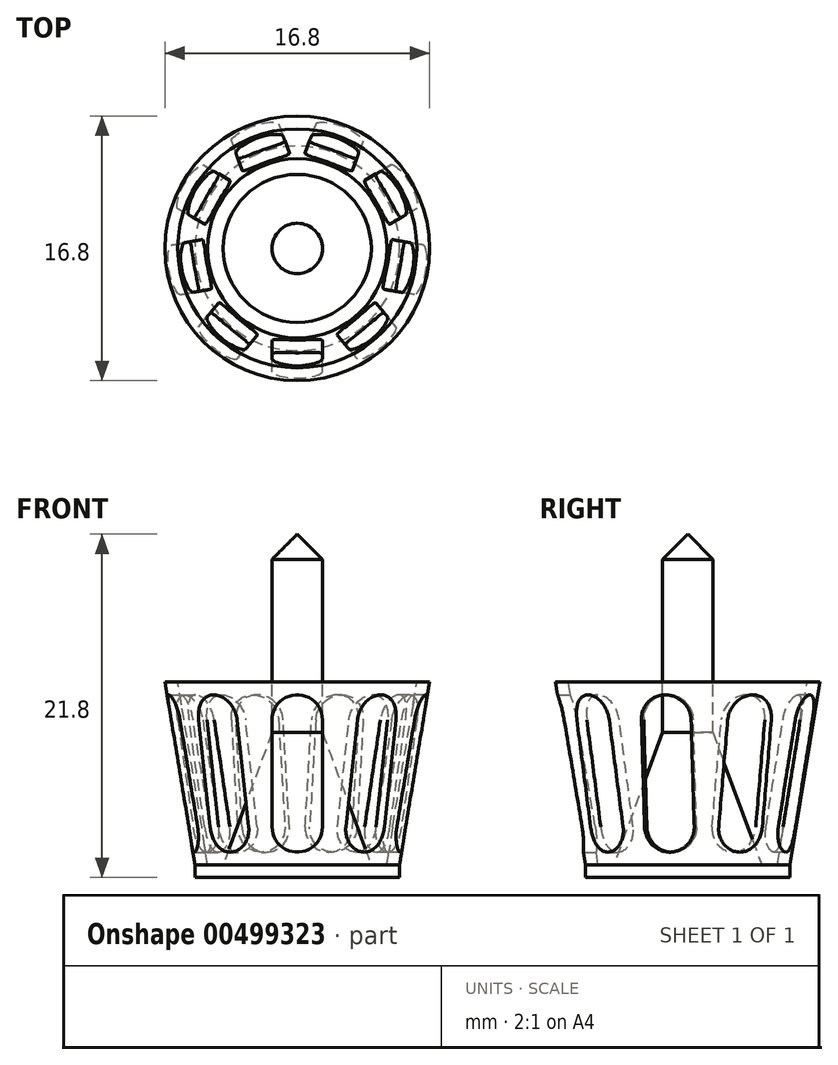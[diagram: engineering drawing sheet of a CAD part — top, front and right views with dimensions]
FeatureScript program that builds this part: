
annotation { "Feature Type Name" : "Feature", "Feature Type Description" : "" }
export const myFeature = defineFeature(function(context is Context, id is Id, definition is map)
    precondition{}
    {
        {
            var Q0;
            Q0=qCreatedBy(makeId("Top.planeOp"),FACE);
            var sketch = newSketch(context, id + "F0", { "sketchPlane" : qUnion([Q0])});
            skCircle(sketch, "E0", {"center": v(0, 0) * mm, "radius": 6.5 * mm});
            skSolve(sketch);
        }
        {
            var Q0;
            Q0=qSketchRegion(id+"F0",true);
            extrude(context, id + "F1", {"entities" : qUnion([Q0]), "depth" : 0.8 * mm});
        }
        {
            var Q0;
            Q0=qCreatedBy(makeId("Front.planeOp"),FACE);
            var sketch = newSketch(context, id + "F2", { "sketchPlane" : qUnion([Q0])});
            skLineSegment(sketch, "E1.0", {"start": v(-6.5, 0.8) * mm, "end": v(6.5, 0.8) * mm, "construction": true});
            skLineSegment(sketch, "E2", {"start": v(0, 0.8) * mm, "end": v(4.7, 0.8) * mm});
            skLineSegment(sketch, "E3", {"start": v(4.7, 0.8) * mm, "end": v(1.6, 9.2) * mm});
            skLineSegment(sketch, "E4", {"start": v(1.6, 9.2) * mm, "end": v(1.6, 20.2) * mm});
            skLineSegment(sketch, "E5", {"start": v(1.6, 20.2) * mm, "end": v(0, 21.8) * mm});
            skLineSegment(sketch, "E6", {"start": v(0, 21.8) * mm, "end": v(0, 0.8) * mm});
            skLineSegment(sketch, "E7", {"start": v(0, 23.8) * mm, "end": v(0, -5.26) * mm, "construction": true});
            skSolve(sketch);
        }
        {
            var Q0;
            Q0=qSketchRegion(id+"F2",true);
            var Q1;
            Q1=sQuery(id+"F2.wireOp",EDGE,"E7");
            revolve(context, id + "F3", {"operationType" : NewBodyOperationType.ADD, "entities" : qUnion([Q0]), "axis" : qUnion([Q1]), "revolveType" : RevolveType.FULL});
        }
        {
            var Q0;
            Q0=qCreatedBy(makeId("Front.planeOp"),FACE);
            var sketch = newSketch(context, id + "F4", { "sketchPlane" : qUnion([Q0])});
            skLineSegment(sketch, "E8.0", {"start": v(-6.5, 0.8) * mm, "end": v(6.5, 0.8) * mm, "construction": true});
            skLineSegment(sketch, "E9", {"start": v(6.5, 0.8) * mm, "end": v(8.4, 12.4) * mm});
            skLineSegment(sketch, "E10", {"start": v(8.4, 12.4) * mm, "end": v(7.59, 12.4) * mm});
            skLineSegment(sketch, "E11", {"start": v(7.59, 12.4) * mm, "end": v(5.69, 0.8) * mm});
            skLineSegment(sketch, "E12", {"start": v(5.69, 0.8) * mm, "end": v(6.5, 0.8) * mm});
            skLineSegment(sketch, "E13", {"start": v(0, 18.23) * mm, "end": v(0, -3.28) * mm, "construction": true});
            skSolve(sketch);
        }
        {
            var Q0;
            Q0=qSketchRegion(id+"F4",true);
            var Q1;
            Q1=qConstructionFilter(qBodyType(qCreatedBy(id+"F4",EDGE),BodyType.WIRE),ConstructionObject.NO);
            var Q2;
            Q2=sQuery(id+"F4.wireOp",EDGE,"E13");
            revolve(context, id + "F5", {"operationType" : NewBodyOperationType.ADD, "entities" : qUnion([Q0]), "surfaceEntities" : qUnion([Q1]), "axis" : qUnion([Q2]), "revolveType" : RevolveType.FULL});
        }
        {
            var Q0;
            Q0=qCreatedBy(makeId("Front.planeOp"),FACE);
            var sketch = newSketch(context, id + "F6", { "sketchPlane" : qUnion([Q0])});
            skLineSegment(sketch, "E14.bottom", {"start": v(0, 11.6) * mm, "end": v(0, 11.6) * mm});
            skLineSegment(sketch, "E14.top", {"start": v(0, 1.6) * mm, "end": v(0, 1.6) * mm});
            skLineSegment(sketch, "E14.left", {"start": v(-1.6, 10) * mm, "end": v(-1.6, 3.2) * mm});
            skLineSegment(sketch, "E14.right", {"start": v(1.6, 10) * mm, "end": v(1.6, 3.2) * mm});
            skLineSegment(sketch, "E15.0", {"start": v(-8.4, 12.4) * mm, "end": v(8.4, 12.4) * mm, "construction": true});
            skLineSegment(sketch, "E16.0", {"start": v(-6.5, 0.8) * mm, "end": v(6.5, 0.8) * mm, "construction": true});
            skPoint(sketch, "E17.visualSharp", {"position": v(-1.6, 11.6) * mm});
            skArc(sketch, "E17.filletArc", {"start": v(0, 11.6) * mm, "mid": v(-1.13, 11.13) * mm, "end": v(-1.6, 10) * mm});
            skPoint(sketch, "E18.visualSharp", {"position": v(1.6, 11.6) * mm});
            skArc(sketch, "E18.filletArc", {"start": v(1.6, 10) * mm, "mid": v(1.13, 11.13) * mm, "end": v(0, 11.6) * mm});
            skPoint(sketch, "E19.visualSharp", {"position": v(-1.6, 1.6) * mm});
            skArc(sketch, "E19.filletArc", {"start": v(-1.6, 3.2) * mm, "mid": v(-1.13, 2.07) * mm, "end": v(0, 1.6) * mm});
            skPoint(sketch, "E20.visualSharp", {"position": v(1.6, 1.6) * mm});
            skArc(sketch, "E20.filletArc", {"start": v(0, 1.6) * mm, "mid": v(1.13, 2.07) * mm, "end": v(1.6, 3.2) * mm});
            skSolve(sketch);
        }
        {
            var Q0;
            Q0=qCreatedBy(makeId("Front.planeOp"),FACE);
            cPlane(context, id + "F7", {"entities" : qUnion([Q0]), "cplaneType" : CPlaneType.OFFSET, "offset" : 5 * mm, "width" : 150 * mm, "height" : 150 * mm});
        }
        {
            var Q0;
            Q0=qCreatedBy(id+"F7.planeOp",FACE);
            var sketch = newSketch(context, id + "F8", { "sketchPlane" : qUnion([Q0])});
            skLineSegment(sketch, "E21.bottom", {"start": v(0, 11.6) * mm, "end": v(0, 11.6) * mm});
            skLineSegment(sketch, "E21.top", {"start": v(0, 1.6) * mm, "end": v(0, 1.6) * mm});
            skLineSegment(sketch, "E21.left", {"start": v(-1.6, 10) * mm, "end": v(-1.6, 3.2) * mm});
            skLineSegment(sketch, "E21.right", {"start": v(1.6, 10) * mm, "end": v(1.6, 3.2) * mm});
            skPoint(sketch, "E22.visualSharp", {"position": v(-1.6, 11.6) * mm});
            skArc(sketch, "E22.filletArc", {"start": v(0, 11.6) * mm, "mid": v(-1.13, 11.13) * mm, "end": v(-1.6, 10) * mm});
            skPoint(sketch, "E23.visualSharp", {"position": v(1.6, 11.6) * mm});
            skArc(sketch, "E23.filletArc", {"start": v(1.6, 10) * mm, "mid": v(1.13, 11.13) * mm, "end": v(0, 11.6) * mm});
            skPoint(sketch, "E24.visualSharp", {"position": v(-1.6, 1.6) * mm});
            skArc(sketch, "E24.filletArc", {"start": v(-1.6, 3.2) * mm, "mid": v(-1.13, 2.07) * mm, "end": v(0, 1.6) * mm});
            skPoint(sketch, "E25.visualSharp", {"position": v(1.6, 1.6) * mm});
            skArc(sketch, "E25.filletArc", {"start": v(0, 1.6) * mm, "mid": v(1.13, 2.07) * mm, "end": v(1.6, 3.2) * mm});
            skSolve(sketch);
        }
        {
            var Q0;
            Q0=makeQuery(id+"F8.imprint","IMPRINT",FACE,{"disambiguationData":[TD([[makeQuery(id+"F8.imprint","IMPRINT",EDGE,{"derivedFrom":sQuery(id+"F8.wireOp",EDGE,"E21.left")}),1.0]])]});
            extrude(context, id + "F9", {"entities" : qUnion([Q0]), "depth" : 10 * mm});
        }
        {
            var Q0;
            Q0=makeQuery(id+"F9.opExtrude","SWEPT_BODY",BODY,{"disambiguationData":[OSD([sQuery(id+"F8.wireOp",EDGE,"E21.left"),sQuery(id+"F8.wireOp",EDGE,"E21.right"),sQuery(id+"F8.wireOp",EDGE,"E22.filletArc"),sQuery(id+"F8.wireOp",EDGE,"E23.filletArc"),sQuery(id+"F8.wireOp",EDGE,"E24.filletArc"),sQuery(id+"F8.wireOp",EDGE,"E25.filletArc")])]});
            var Q1;
            Q1=makeQuery(id+"F3.opRevolve","SWEPT_FACE",FACE,{"disambiguationData":[OSD([sQuery(id+"F2.wireOp",EDGE,"E4")])]});
            circularPattern(context, id + "F10", {"entities" : qUnion([Q0]), "axis" : qUnion([Q1]), "angle" : 360 * degree, "instanceCount" : 9, "equalSpace" : true});
        }
        {
            var Q0;
            Q0=makeQuery(id+"F9.opExtrude","SWEPT_BODY",BODY,{"disambiguationData":[OSD([sQuery(id+"F8.wireOp",EDGE,"E21.left"),sQuery(id+"F8.wireOp",EDGE,"E21.right"),sQuery(id+"F8.wireOp",EDGE,"E22.filletArc"),sQuery(id+"F8.wireOp",EDGE,"E23.filletArc"),sQuery(id+"F8.wireOp",EDGE,"E24.filletArc"),sQuery(id+"F8.wireOp",EDGE,"E25.filletArc")])]});
            var Q1;
            Q1=makeQuery(id+"F10.opPattern","COPY",BODY,{"derivedFrom":makeQuery(id+"F9.opExtrude","SWEPT_BODY",BODY,{"disambiguationData":[OSD([sQuery(id+"F8.wireOp",EDGE,"E21.left"),sQuery(id+"F8.wireOp",EDGE,"E21.right"),sQuery(id+"F8.wireOp",EDGE,"E22.filletArc"),sQuery(id+"F8.wireOp",EDGE,"E23.filletArc"),sQuery(id+"F8.wireOp",EDGE,"E24.filletArc"),sQuery(id+"F8.wireOp",EDGE,"E25.filletArc")])]}),"instanceName":"1"});
            var Q2;
            Q2=makeQuery(id+"F10.opPattern","COPY",BODY,{"derivedFrom":makeQuery(id+"F9.opExtrude","SWEPT_BODY",BODY,{"disambiguationData":[OSD([sQuery(id+"F8.wireOp",EDGE,"E21.left"),sQuery(id+"F8.wireOp",EDGE,"E21.right"),sQuery(id+"F8.wireOp",EDGE,"E22.filletArc"),sQuery(id+"F8.wireOp",EDGE,"E23.filletArc"),sQuery(id+"F8.wireOp",EDGE,"E24.filletArc"),sQuery(id+"F8.wireOp",EDGE,"E25.filletArc")])]}),"instanceName":"2"});
            var Q3;
            Q3=makeQuery(id+"F10.opPattern","COPY",BODY,{"derivedFrom":makeQuery(id+"F9.opExtrude","SWEPT_BODY",BODY,{"disambiguationData":[OSD([sQuery(id+"F8.wireOp",EDGE,"E21.left"),sQuery(id+"F8.wireOp",EDGE,"E21.right"),sQuery(id+"F8.wireOp",EDGE,"E22.filletArc"),sQuery(id+"F8.wireOp",EDGE,"E23.filletArc"),sQuery(id+"F8.wireOp",EDGE,"E24.filletArc"),sQuery(id+"F8.wireOp",EDGE,"E25.filletArc")])]}),"instanceName":"3"});
            var Q4;
            Q4=makeQuery(id+"F10.opPattern","COPY",BODY,{"derivedFrom":makeQuery(id+"F9.opExtrude","SWEPT_BODY",BODY,{"disambiguationData":[OSD([sQuery(id+"F8.wireOp",EDGE,"E21.left"),sQuery(id+"F8.wireOp",EDGE,"E21.right"),sQuery(id+"F8.wireOp",EDGE,"E22.filletArc"),sQuery(id+"F8.wireOp",EDGE,"E23.filletArc"),sQuery(id+"F8.wireOp",EDGE,"E24.filletArc"),sQuery(id+"F8.wireOp",EDGE,"E25.filletArc")])]}),"instanceName":"4"});
            var Q5;
            Q5=makeQuery(id+"F10.opPattern","COPY",BODY,{"derivedFrom":makeQuery(id+"F9.opExtrude","SWEPT_BODY",BODY,{"disambiguationData":[OSD([sQuery(id+"F8.wireOp",EDGE,"E21.left"),sQuery(id+"F8.wireOp",EDGE,"E21.right"),sQuery(id+"F8.wireOp",EDGE,"E22.filletArc"),sQuery(id+"F8.wireOp",EDGE,"E23.filletArc"),sQuery(id+"F8.wireOp",EDGE,"E24.filletArc"),sQuery(id+"F8.wireOp",EDGE,"E25.filletArc")])]}),"instanceName":"5"});
            var Q6;
            Q6=makeQuery(id+"F10.opPattern","COPY",BODY,{"derivedFrom":makeQuery(id+"F9.opExtrude","SWEPT_BODY",BODY,{"disambiguationData":[OSD([sQuery(id+"F8.wireOp",EDGE,"E21.left"),sQuery(id+"F8.wireOp",EDGE,"E21.right"),sQuery(id+"F8.wireOp",EDGE,"E22.filletArc"),sQuery(id+"F8.wireOp",EDGE,"E23.filletArc"),sQuery(id+"F8.wireOp",EDGE,"E24.filletArc"),sQuery(id+"F8.wireOp",EDGE,"E25.filletArc")])]}),"instanceName":"6"});
            var Q7;
            Q7=makeQuery(id+"F10.opPattern","COPY",BODY,{"derivedFrom":makeQuery(id+"F9.opExtrude","SWEPT_BODY",BODY,{"disambiguationData":[OSD([sQuery(id+"F8.wireOp",EDGE,"E21.left"),sQuery(id+"F8.wireOp",EDGE,"E21.right"),sQuery(id+"F8.wireOp",EDGE,"E22.filletArc"),sQuery(id+"F8.wireOp",EDGE,"E23.filletArc"),sQuery(id+"F8.wireOp",EDGE,"E24.filletArc"),sQuery(id+"F8.wireOp",EDGE,"E25.filletArc")])]}),"instanceName":"7"});
            var Q8;
            Q8=makeQuery(id+"F10.opPattern","COPY",BODY,{"derivedFrom":makeQuery(id+"F9.opExtrude","SWEPT_BODY",BODY,{"disambiguationData":[OSD([sQuery(id+"F8.wireOp",EDGE,"E21.left"),sQuery(id+"F8.wireOp",EDGE,"E21.right"),sQuery(id+"F8.wireOp",EDGE,"E22.filletArc"),sQuery(id+"F8.wireOp",EDGE,"E23.filletArc"),sQuery(id+"F8.wireOp",EDGE,"E24.filletArc"),sQuery(id+"F8.wireOp",EDGE,"E25.filletArc")])]}),"instanceName":"8"});
            var Q9;
            Q9=makeQuery(id+"F1.opExtrude","SWEPT_BODY",BODY,{"disambiguationData":[OSD([sQuery(id+"F0.wireOp",EDGE,"E0")])]});
            booleanBodies(context, id + "F11", {"operationType" : BooleanOperationType.SUBTRACTION, "tools" : qUnion([Q0, Q1, Q2, Q3, Q4, Q5, Q6, Q7, Q8]), "targets" : qUnion([Q9])});
        }
    });
